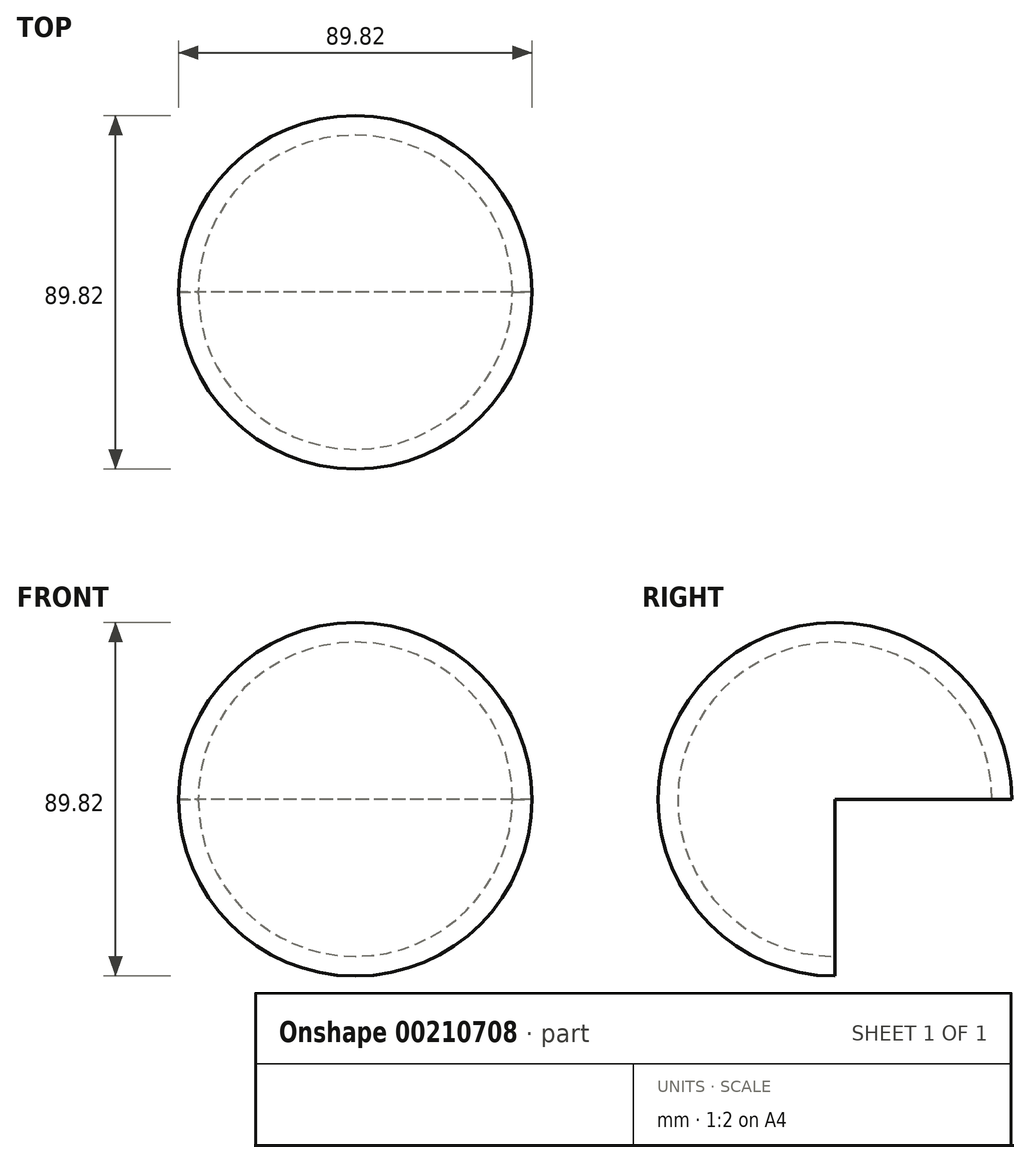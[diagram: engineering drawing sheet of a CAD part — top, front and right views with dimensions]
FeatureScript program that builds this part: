
annotation { "Feature Type Name" : "Feature", "Feature Type Description" : "" }
export const myFeature = defineFeature(function(context is Context, id is Id, definition is map)
    precondition{}
    {
        {
            var Q0;
            Q0=qCreatedBy(makeId("Top.planeOp"),FACE);
            var sketch = newSketch(context, id + "F0", { "sketchPlane" : qUnion([Q0])});
            skArc(sketch, "E0", {"start": v(44.91, 0) * mm, "mid": v(0, 44.91) * mm, "end": v(-44.91, 0) * mm});
            skLineSegment(sketch, "E1", {"start": v(-44.91, 0) * mm, "end": v(44.91, 0) * mm});
            skSolve(sketch);
        }
        {
            var Q0;
            Q0=makeQuery(id+"F0.imprint","IMPRINT",FACE,{"disambiguationData":[TD([[makeQuery(id+"F0.imprint","IMPRINT",EDGE,{"derivedFrom":sQuery(id+"F0.wireOp",EDGE,"E0")}),1.0]])]});
            var Q1;
            Q1=sQuery(id+"F0.wireOp",EDGE,"E1");
            revolve(context, id + "F1", {"entities" : qUnion([Q0]), "axis" : qUnion([Q1]), "revolveType" : RevolveType.ONE_DIRECTION, "angle" : 270 * degree});
        }
        {
            var Q0;
            Q0=makeQuery(id+"F1.opRevolve","CAP_FACE",FACE,{"disambiguationData":[OSD([sQuery(id+"F0.wireOp",EDGE,"E0"),sQuery(id+"F0.wireOp",EDGE,"E1")])],"isStart":false});
            var Q1;
            Q1=makeQuery(id+"F1.opRevolve","CAP_FACE",FACE,{"disambiguationData":[OSD([sQuery(id+"F0.wireOp",EDGE,"E0"),sQuery(id+"F0.wireOp",EDGE,"E1")])],"isStart":true});
            shell(context, id + "F2", {"entities" : qUnion([Q0, Q1]), "thickness" : 5 * mm});
        }
    });
